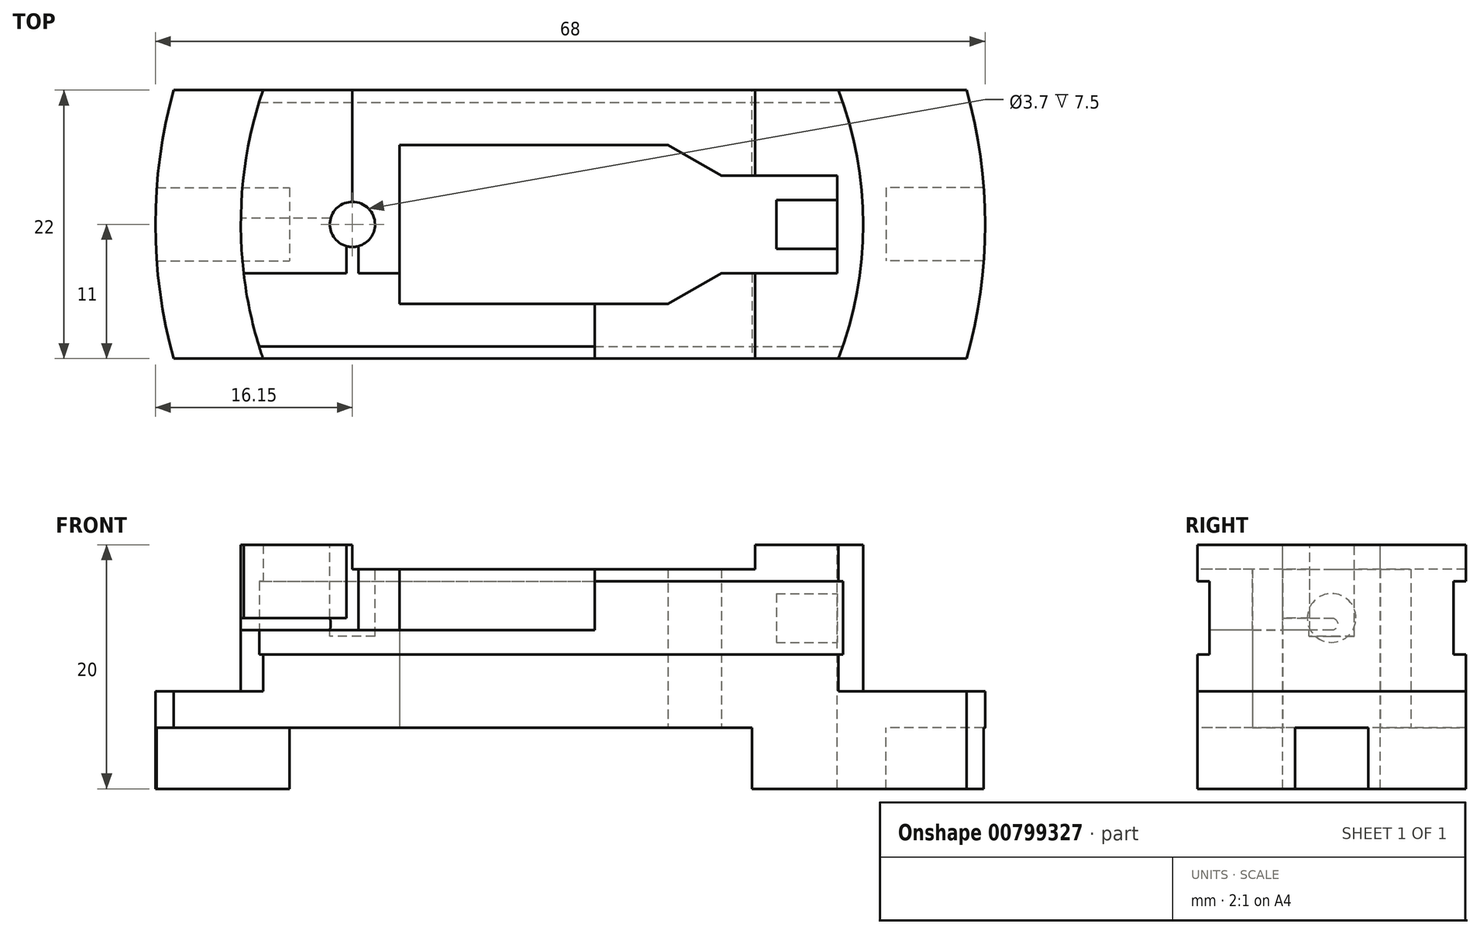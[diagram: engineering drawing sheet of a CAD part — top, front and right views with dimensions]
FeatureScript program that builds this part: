
annotation { "Feature Type Name" : "Feature", "Feature Type Description" : "" }
export const myFeature = defineFeature(function(context is Context, id is Id, definition is map)
    precondition{}
    {
        {
            var Q0;
            Q0=qCreatedBy(makeId("Top.planeOp"),FACE);
            var sketch = newSketch(context, id + "F0", { "sketchPlane" : qUnion([Q0])});
            skLineSegment(sketch, "E0.bottom", {"start": v(32.5, 11) * mm, "end": v(-32.5, 11) * mm});
            skLineSegment(sketch, "E0.top", {"start": v(32.5, -11) * mm, "end": v(-32.5, -11) * mm});
            skLineSegment(sketch, "E0.left", {"start": v(32.5, 11) * mm, "end": v(32.5, -11) * mm, "construction": true});
            skLineSegment(sketch, "E0.right", {"start": v(-32.5, 11) * mm, "end": v(-32.5, -11) * mm, "construction": true});
            skPoint(sketch, "E0.middle", {"position": v(0, 0) * mm});
            skArc(sketch, "E1", {"start": v(-32.5, 11) * mm, "mid": v(-34, 0) * mm, "end": v(-32.5, -11) * mm});
            skArc(sketch, "E2", {"start": v(32.5, -11) * mm, "mid": v(34, 0) * mm, "end": v(32.5, 11) * mm});
            skSolve(sketch);
        }
        {
            var Q0;
            Q0 = qSketchRegion(id + "F0", true);
            var Q1;
            Q1 = qConstructionFilter(qBodyType(qCreatedBy(id + "F0" ,EDGE), BodyType.WIRE), ConstructionObject.NO);
            extrude(context, id + "F1", {"entities" : qUnion([Q0]), "surfaceEntities" : qUnion([Q1]), "oppositeDirection" : true, "depth" : 3 * mm, "offsetDistance" : 25 * mm});
        }
        {
            var Q0;
            Q0=makeQuery(id+"F1.opExtrude","CAP_FACE",FACE,{"disambiguationData":[OSD([sQuery(id+"F0.wireOp",EDGE,"E0.bottom"),sQuery(id+"F0.wireOp",EDGE,"E0.top"),sQuery(id+"F0.wireOp",EDGE,"E1"),sQuery(id+"F0.wireOp",EDGE,"E2")])],"isStart":false});
            var sketch = newSketch(context, id + "F2", { "sketchPlane" : qUnion([Q0])});
            skLineSegment(sketch, "E3", {"start": v(33.9, 3) * mm, "end": v(25.9, 3) * mm});
            skLineSegment(sketch, "E4", {"start": v(25.9, 3) * mm, "end": v(25.9, 0) * mm});
            skLineSegment(sketch, "E5", {"start": v(21.9, 0) * mm, "end": v(21.9, 4) * mm});
            skLineSegment(sketch, "E6", {"start": v(21.9, 4) * mm, "end": v(14.9, 4) * mm});
            skLineSegment(sketch, "E7", {"start": v(14.9, 4) * mm, "end": v(14.9, 11) * mm});
            skLineSegment(sketch, "E8", {"start": v(-33.9, 3) * mm, "end": v(-23, 3) * mm});
            skLineSegment(sketch, "E9", {"start": v(-23, 3) * mm, "end": v(-23, 0) * mm});
            skLineSegment(sketch, "E10.0", {"start": v(32.5, 11) * mm, "end": v(14.9, 11) * mm});
            skArc(sketch, "E11.0", {"start": v(32.5, 11) * mm, "mid": v(33.4, 7.03) * mm, "end": v(33.9, 3) * mm});
            skArc(sketch, "E12.0", {"start": v(-32.5, -11) * mm, "mid": v(-34, 0) * mm, "end": v(-32.5, 11) * mm});
            skLineSegment(sketch, "E13.0", {"start": v(32.5, -11) * mm, "end": v(14.9, -11) * mm});
            skLineSegment(sketch, "E14.MirrorCS", {"start": v(-33.9, -3) * mm, "end": v(-23, -3) * mm});
            skLineSegment(sketch, "E15.MirrorCS", {"start": v(-23, -3) * mm, "end": v(-23, 0) * mm});
            skLineSegment(sketch, "E16.MirrorCS", {"start": v(14.9, -4) * mm, "end": v(14.9, -11) * mm});
            skLineSegment(sketch, "E17.MirrorCS", {"start": v(21.9, -4) * mm, "end": v(14.9, -4) * mm});
            skLineSegment(sketch, "E18.MirrorCS", {"start": v(21.9, 0) * mm, "end": v(21.9, -4) * mm});
            skLineSegment(sketch, "E19.MirrorCS", {"start": v(25.9, -3) * mm, "end": v(25.9, 0) * mm});
            skLineSegment(sketch, "E20.MirrorCS", {"start": v(33.9, -3) * mm, "end": v(25.9, -3) * mm});
            skArc(sketch, "E21.trimOffspring", {"start": v(33.9, -3) * mm, "mid": v(33.4, -7.03) * mm, "end": v(32.5, -11) * mm});
            skSolve(sketch);
        }
        {
            var Q0;
            {var subQ2=sQuery(id+"F2.wireOp",EDGE,"E8");Q0=makeQuery(id+"F2.imprint","IMPRINT",FACE,{"disambiguationData":[TD([[makeQuery(id+"F2.imprint","IMPRINT",EDGE,{"derivedFrom":subQ2}),-1.0]])]});}
            var Q1;
            Q1=makeQuery(id+"F2.imprint","IMPRINT",FACE,{"disambiguationData":[TD([[makeQuery(id+"F2.imprint","IMPRINT",EDGE,{"derivedFrom":sQuery(id+"F2.wireOp",EDGE,"E3")}),-1.0]])]});
            extrude(context, id + "F3", {"entities" : qUnion([Q0, Q1]), "operationType" : NewBodyOperationType.ADD, "depth" : 5 * mm, "offsetDistance" : 25 * mm});
        }
        {
            var Q0;
            {var subQ0=sQuery(id+"F0.wireOp",EDGE,"E0.bottom");var subQ1=sQuery(id+"F0.wireOp",EDGE,"E0.top");var subQ2=sQuery(id+"F0.wireOp",EDGE,"E1");Q0=makeQuery(id+"F3.boolean.opBoolean","SPLIT",FACE,{"disambiguationData":[TD([makeQuery(id+"F1.opExtrude","SWEPT_FACE",FACE,{"disambiguationData":[OSD([subQ0])]})])],"derivedFrom":makeQuery(id+"F1.opExtrude","CAP_FACE",FACE,{"disambiguationData":[OSD([subQ0,subQ1,subQ2,sQuery(id+"F0.wireOp",EDGE,"E2")])],"isStart":false})});}
            var sketch = newSketch(context, id + "F4", { "sketchPlane" : qUnion([Q0])});
            skLineSegment(sketch, "E22.0", {"start": v(21.9, 4) * mm, "end": v(14.9, 4) * mm});
            skLineSegment(sketch, "E23.0", {"start": v(21.9, -4) * mm, "end": v(21.9, 4) * mm});
            skLineSegment(sketch, "E24.0", {"start": v(21.9, -4) * mm, "end": v(14.9, -4) * mm});
            skLineSegment(sketch, "E25", {"start": v(-14, 0) * mm, "end": v(-14, 6.5) * mm});
            skLineSegment(sketch, "E26", {"start": v(-14, 6.5) * mm, "end": v(8, 6.5) * mm});
            skLineSegment(sketch, "E27", {"start": v(8, 6.5) * mm, "end": v(12.4, 4) * mm});
            skLineSegment(sketch, "E28", {"start": v(12.4, 4) * mm, "end": v(14.9, 4) * mm});
            skLineSegment(sketch, "E29.MirrorCS", {"start": v(-14, 0) * mm, "end": v(-14, -6.5) * mm});
            skLineSegment(sketch, "E30.MirrorCS", {"start": v(-14, -6.5) * mm, "end": v(8, -6.5) * mm});
            skLineSegment(sketch, "E31.MirrorCS", {"start": v(8, -6.5) * mm, "end": v(12.4, -4) * mm});
            skLineSegment(sketch, "E32.MirrorCS", {"start": v(12.4, -4) * mm, "end": v(14.9, -4) * mm});
            skSolve(sketch);
        }
        {
            var Q0;
            Q0=makeQuery(id+"F4.imprint","IMPRINT",FACE,{"disambiguationData":[TD([[makeQuery(id+"F4.imprint","IMPRINT",EDGE,{"derivedFrom":sQuery(id+"F4.wireOp",EDGE,"E22.0")}),1.0]])]});
            extrude(context, id + "F5", {"entities" : qUnion([Q0]), "operationType" : NewBodyOperationType.REMOVE, "endBound" : BoundingType.THROUGH_ALL, "oppositeDirection" : true, "depth" : 25 * mm, "offsetDistance" : 25 * mm});
        }
        {
            var Q0;
            Q0=makeQuery(id+"F1.opExtrude","CAP_FACE",FACE,{"disambiguationData":[OSD([sQuery(id+"F0.wireOp",EDGE,"E0.bottom"),sQuery(id+"F0.wireOp",EDGE,"E0.top"),sQuery(id+"F0.wireOp",EDGE,"E1"),sQuery(id+"F0.wireOp",EDGE,"E2")])],"isStart":true});
            var sketch = newSketch(context, id + "F6", { "sketchPlane" : qUnion([Q0])});
            skArc(sketch, "E33", {"start": v(-25.18, 11) * mm, "mid": v(-27, 0) * mm, "end": v(-25.18, -11) * mm});
            skArc(sketch, "E34", {"start": v(21.99, -11) * mm, "mid": v(24, 0) * mm, "end": v(21.99, 11) * mm});
            skLineSegment(sketch, "E35.0", {"start": v(21.99, 11) * mm, "end": v(-25.18, 11) * mm});
            skLineSegment(sketch, "E36.0", {"start": v(21.99, -11) * mm, "end": v(-25.18, -11) * mm});
            skPoint(sketch, "E37.orphan", {"position": v(-32.5, 11) * mm});
            skPoint(sketch, "E38.orphan", {"position": v(32.5, 11) * mm});
            skPoint(sketch, "E39.orphan", {"position": v(32.5, -11) * mm});
            skPoint(sketch, "E40.orphan", {"position": v(-32.5, -11) * mm});
            skSolve(sketch);
        }
        {
            var Q0;
            Q0=makeQuery(id+"F6.imprint","IMPRINT",FACE,{"disambiguationData":[TD([[makeQuery(id+"F6.imprint","IMPRINT",EDGE,{"derivedFrom":sQuery(id+"F6.wireOp",EDGE,"E33")}),1.0]])]});
            extrude(context, id + "F7", {"entities" : qUnion([Q0]), "operationType" : NewBodyOperationType.ADD, "depth" : 12 * mm, "offsetDistance" : 25 * mm});
        }
        {
            var Q0;
            Q0=qCreatedBy(makeId("Right.planeOp"),FACE);
            var sketch = newSketch(context, id + "F8", { "sketchPlane" : qUnion([Q0])});
            skLineSegment(sketch, "E41.0", {"start": v(-11, 9) * mm, "end": v(-11, 3) * mm});
            skLineSegment(sketch, "E42.0", {"start": v(11, 9) * mm, "end": v(11, 3) * mm});
            skLineSegment(sketch, "E43", {"start": v(-11, 9) * mm, "end": v(-10, 9) * mm});
            skLineSegment(sketch, "E44", {"start": v(-10, 9) * mm, "end": v(-10, 3) * mm});
            skLineSegment(sketch, "E45", {"start": v(-10, 3) * mm, "end": v(-11, 3) * mm});
            skPoint(sketch, "E46.orphan", {"position": v(-11, 12) * mm});
            skPoint(sketch, "E47.orphan", {"position": v(-11, 0) * mm});
            skLineSegment(sketch, "E48.MirrorCS", {"start": v(11, 9) * mm, "end": v(10, 9) * mm});
            skLineSegment(sketch, "E49.MirrorCS", {"start": v(10, 9) * mm, "end": v(10, 3) * mm});
            skLineSegment(sketch, "E50.MirrorCS", {"start": v(10, 3) * mm, "end": v(11, 3) * mm});
            skPoint(sketch, "E51.orphan", {"position": v(11, 12) * mm});
            skPoint(sketch, "E52.orphan", {"position": v(11, 0) * mm});
            skSolve(sketch);
        }
        {
            var Q0;
            Q0 = qSketchRegion(id + "F8", true);
            extrude(context, id + "F9", {"entities" : qUnion([Q0]), "operationType" : NewBodyOperationType.REMOVE, "endBound" : BoundingType.THROUGH_ALL, "oppositeDirection" : true, "depth" : 25 * mm, "offsetDistance" : 25 * mm, "hasSecondDirection" : true, "secondDirectionBound" : SecondDirectionBoundingType.THROUGH_ALL, "secondDirectionOppositeDirection" : false, "secondDirectionDepth" : 25 * mm});
        }
        {
            var Q0;
            Q0=makeQuery(id+"F7.opExtrude","CAP_FACE",FACE,{"disambiguationData":[OSD([sQuery(id+"F0.wireOp",EDGE,"E0.bottom"),sQuery(id+"F0.wireOp",EDGE,"E0.top"),sQuery(id+"F0.wireOp",EDGE,"E1"),sQuery(id+"F0.wireOp",EDGE,"E2"),sQuery(id+"F4.wireOp",EDGE,"E22.0"),sQuery(id+"F4.wireOp",EDGE,"E23.0"),sQuery(id+"F4.wireOp",EDGE,"E24.0"),sQuery(id+"F4.wireOp",EDGE,"E25"),sQuery(id+"F4.wireOp",EDGE,"E26"),sQuery(id+"F4.wireOp",EDGE,"E27"),sQuery(id+"F4.wireOp",EDGE,"E28"),sQuery(id+"F4.wireOp",EDGE,"E29.MirrorCS"),sQuery(id+"F4.wireOp",EDGE,"E30.MirrorCS"),sQuery(id+"F4.wireOp",EDGE,"E31.MirrorCS"),sQuery(id+"F4.wireOp",EDGE,"E32.MirrorCS"),sQuery(id+"F6.wireOp",EDGE,"E33"),sQuery(id+"F6.wireOp",EDGE,"E34"),sQuery(id+"F6.wireOp",EDGE,"E35.0"),sQuery(id+"F6.wireOp",EDGE,"E36.0")])],"isStart":false});
            var sketch = newSketch(context, id + "F10", { "sketchPlane" : qUnion([Q0])});
            skCircle(sketch, "E53", {"center": v(-17.85, 0) * mm, "radius": 1.85 * mm});
            skSolve(sketch);
        }
        {
            var Q0;
            Q0=makeQuery(id+"F10.imprint","IMPRINT",FACE,{"disambiguationData":[TD([[makeQuery(id+"F10.imprint","IMPRINT",EDGE,{"derivedFrom":sQuery(id+"F10.wireOp",EDGE,"E53")}),1.0]])]});
            extrude(context, id + "F11", {"entities" : qUnion([Q0]), "operationType" : NewBodyOperationType.REMOVE, "oppositeDirection" : true, "depth" : 7.5 * mm, "offsetDistance" : 25 * mm});
        }
        {
            var Q0;
            Q0=makeQuery(id+"F7.opExtrude","CAP_FACE",FACE,{"disambiguationData":[OSD([sQuery(id+"F0.wireOp",EDGE,"E0.bottom"),sQuery(id+"F0.wireOp",EDGE,"E0.top"),sQuery(id+"F0.wireOp",EDGE,"E1"),sQuery(id+"F0.wireOp",EDGE,"E2"),sQuery(id+"F4.wireOp",EDGE,"E22.0"),sQuery(id+"F4.wireOp",EDGE,"E23.0"),sQuery(id+"F4.wireOp",EDGE,"E24.0"),sQuery(id+"F4.wireOp",EDGE,"E25"),sQuery(id+"F4.wireOp",EDGE,"E26"),sQuery(id+"F4.wireOp",EDGE,"E27"),sQuery(id+"F4.wireOp",EDGE,"E28"),sQuery(id+"F4.wireOp",EDGE,"E29.MirrorCS"),sQuery(id+"F4.wireOp",EDGE,"E30.MirrorCS"),sQuery(id+"F4.wireOp",EDGE,"E31.MirrorCS"),sQuery(id+"F4.wireOp",EDGE,"E32.MirrorCS"),sQuery(id+"F6.wireOp",EDGE,"E33"),sQuery(id+"F6.wireOp",EDGE,"E34"),sQuery(id+"F6.wireOp",EDGE,"E35.0"),sQuery(id+"F6.wireOp",EDGE,"E36.0")])],"isStart":false});
            var sketch = newSketch(context, id + "F12", { "sketchPlane" : qUnion([Q0])});
            skLineSegment(sketch, "E54.bottom", {"start": v(-17.85, 11) * mm, "end": v(15.15, 11) * mm});
            skLineSegment(sketch, "E54.top", {"start": v(-17.85, -11) * mm, "end": v(15.15, -11) * mm});
            skLineSegment(sketch, "E54.left", {"start": v(-17.85, 11) * mm, "end": v(-17.85, -11) * mm});
            skLineSegment(sketch, "E54.right", {"start": v(15.15, 11) * mm, "end": v(15.15, -11) * mm});
            skPoint(sketch, "E55", {"position": v(-17.85, 0) * mm});
            skLineSegment(sketch, "E56.bottom", {"start": v(-27, -4) * mm, "end": v(2, -4) * mm});
            skLineSegment(sketch, "E56.top", {"start": v(-27, -11) * mm, "end": v(2, -11) * mm});
            skLineSegment(sketch, "E56.left", {"start": v(-27, -4) * mm, "end": v(-27, -11) * mm});
            skLineSegment(sketch, "E56.right", {"start": v(2, -4) * mm, "end": v(2, -11) * mm});
            skLineSegment(sketch, "E57", {"start": v(-17.85, 0) * mm, "end": v(-18.35, 0) * mm});
            skLineSegment(sketch, "E58", {"start": v(-18.35, 0) * mm, "end": v(-18.35, -4) * mm});
            skLineSegment(sketch, "E59.MirrorCS", {"start": v(-17.35, 0) * mm, "end": v(-17.35, -4) * mm});
            skLineSegment(sketch, "E60.MirrorCS", {"start": v(-17.85, 0) * mm, "end": v(-17.35, 0) * mm});
            skSolve(sketch);
        }
        {
            var Q0;
            {var subQ1=sQuery(id+"F12.wireOp",EDGE,"E54.bottom");Q0=makeQuery(id+"F12.imprint","IMPRINT",FACE,{"disambiguationData":[TD([[makeQuery(id+"F12.imprint","IMPRINT",EDGE,{"derivedFrom":subQ1}),1.0]])]});}
            var Q1;
            {var subQ1=sQuery(id+"F12.wireOp",EDGE,"E56.top");var subQ9=sQuery(id+"F12.wireOp",EDGE,"E54.left");var subQ10=makeQuery(id+"F12.imprint","INTERSECT",VERTEX,{"derivedFrom":[subQ9,subQ1]});Q1=makeQuery(id+"F12.imprint","IMPRINT",FACE,{"disambiguationData":[TD([[makeQuery(id+"F12.imprint","IMPRINT",EDGE,{"disambiguationData":[TD([[subQ10,1.0]])],"derivedFrom":subQ9}),1.0]])]});}
            var Q2;
            {var subQ6=sQuery(id+"F12.wireOp",EDGE,"E54.top");Q2=makeQuery(id+"F12.imprint","IMPRINT",FACE,{"disambiguationData":[TD([[makeQuery(id+"F12.imprint","IMPRINT",EDGE,{"derivedFrom":subQ6}),-1.0]])]});}
            extrude(context, id + "F13", {"entities" : qUnion([Q0, Q1, Q2]), "operationType" : NewBodyOperationType.REMOVE, "oppositeDirection" : true, "depth" : 2 * mm, "offsetDistance" : 25 * mm});
        }
        {
            var Q0;
            {var subQ1=sQuery(id+"F12.wireOp",EDGE,"E56.top");var subQ9=sQuery(id+"F12.wireOp",EDGE,"E54.left");var subQ10=makeQuery(id+"F12.imprint","INTERSECT",VERTEX,{"derivedFrom":[subQ9,subQ1]});Q0=makeQuery(id+"F12.imprint","IMPRINT",FACE,{"disambiguationData":[TD([[makeQuery(id+"F12.imprint","IMPRINT",EDGE,{"disambiguationData":[TD([[subQ10,1.0]])],"derivedFrom":subQ9}),1.0]])]});}
            var Q1;
            {var subQ0=sQuery(id+"F12.wireOp",EDGE,"E56.top");var subQ1=sQuery(id+"F12.wireOp",EDGE,"E54.left");var subQ2=makeQuery(id+"F12.imprint","INTERSECT",VERTEX,{"derivedFrom":[subQ1,subQ0]});Q1=makeQuery(id+"F12.imprint","IMPRINT",FACE,{"disambiguationData":[TD([[makeQuery(id+"F12.imprint","IMPRINT",EDGE,{"disambiguationData":[TD([[subQ2,1.0]])],"derivedFrom":subQ1}),-1.0]])]});}
            var Q2;
            {var subQ0=sQuery(id+"F12.wireOp",EDGE,"E56.bottom");var subQ1=sQuery(id+"F12.wireOp",EDGE,"E54.left");var subQ2=makeQuery(id+"F12.imprint","INTERSECT",VERTEX,{"derivedFrom":[subQ1,subQ0]});Q2=makeQuery(id+"F12.imprint","IMPRINT",FACE,{"disambiguationData":[TD([[makeQuery(id+"F12.imprint","IMPRINT",EDGE,{"disambiguationData":[TD([[subQ2,1.0]])],"derivedFrom":subQ1}),1.0]])]});}
            var Q3;
            {var subQ0=sQuery(id+"F12.wireOp",EDGE,"E56.bottom");var subQ1=sQuery(id+"F12.wireOp",EDGE,"E54.left");var subQ2=makeQuery(id+"F12.imprint","INTERSECT",VERTEX,{"derivedFrom":[subQ1,subQ0]});Q3=makeQuery(id+"F12.imprint","IMPRINT",FACE,{"disambiguationData":[TD([[makeQuery(id+"F12.imprint","IMPRINT",EDGE,{"disambiguationData":[TD([[subQ2,1.0]])],"derivedFrom":subQ1}),-1.0]])]});}
            extrude(context, id + "F14", {"entities" : qUnion([Q0, Q1, Q2, Q3]), "operationType" : NewBodyOperationType.REMOVE, "oppositeDirection" : true, "depth" : 7 * mm, "offsetDistance" : 25 * mm});
        }
        {
            var Q0;
            Q0=makeQuery(id+"F1.opExtrude","CAP_EDGE",EDGE,{"disambiguationData":[OSD([sQuery(id+"F0.wireOp",EDGE,"E1")])],"isStart":true});
            cPoint(context, id + "F15", {"entities" : qUnion([Q0]), "parameter" : 0.5});
        }
        {
            var Q0;
            Q0=qCreatedBy(makeId("Right.planeOp"),FACE);
            var Q1;
            Q1 = qCreatedBy(id + "F15" ,VERTEX);
            cPlane(context, id + "F16", {"entities" : qUnion([Q0, Q1]), "cplaneType" : CPlaneType.PLANE_POINT, "offset" : 25 * mm, "width" : 150 * mm, "height" : 150 * mm});
        }
        {
            var Q0;
            Q0=qCreatedBy(id+"F16.planeOp",FACE);
            var sketch = newSketch(context, id + "F17", { "sketchPlane" : qUnion([Q0])});
            skLineSegment(sketch, "E61.0", {"start": v(-4, 5) * mm, "end": v(-10, 5) * mm});
            skLineSegment(sketch, "E62", {"start": v(-4, 5) * mm, "end": v(0, 5) * mm});
            skArc(sketch, "E63", {"start": v(0, 5) * mm, "mid": v(0.5, 5.5) * mm, "end": v(0, 6) * mm});
            skLineSegment(sketch, "E64", {"start": v(0, 6) * mm, "end": v(-4, 6) * mm});
            skLineSegment(sketch, "E65", {"start": v(-4, 6) * mm, "end": v(-4, 5) * mm});
            skSolve(sketch);
        }
        {
            var Q0;
            Q0 = qSketchRegion(id + "F17", true);
            var Q1;
            Q1=makeQuery(id+"F14.boolean.opBoolean","COPY",FACE,{"derivedFrom":makeQuery(id+"F14.opExtrude","SWEPT_FACE",FACE,{"disambiguationData":[OSD([sQuery(id+"F12.wireOp",EDGE,"E59.MirrorCS")])]})});
            extrude(context, id + "F18", {"entities" : qUnion([Q0]), "operationType" : NewBodyOperationType.REMOVE, "endBound" : BoundingType.UP_TO_SURFACE, "depth" : 25 * mm, "endBoundEntityFace" : qUnion([Q1]), "offsetDistance" : 25 * mm});
        }
        {
            var Q0;
            {var subQ0=sQuery(id+"F4.wireOp",EDGE,"E23.0");Q0=makeQuery(id+"F7.boolean.opBoolean","MERGE",FACE,{"derivedFrom":[makeQuery(id+"F5.boolean.opBoolean","MERGE",FACE,{"derivedFrom":[makeQuery(id+"F3.opExtrude","SWEPT_FACE",FACE,{"disambiguationData":[OSD([sQuery(id+"F2.wireOp",EDGE,"E5"),sQuery(id+"F2.wireOp",EDGE,"E18.MirrorCS")])]}),makeQuery(id+"F5.opExtrude","SWEPT_FACE",FACE,{"disambiguationData":[OSD([subQ0])]})]}),makeQuery(id+"F7.opExtrude","SWEPT_FACE",FACE,{"disambiguationData":[OSD([sQuery(id+"F0.wireOp",EDGE,"E0.bottom"),sQuery(id+"F0.wireOp",EDGE,"E0.top"),sQuery(id+"F0.wireOp",EDGE,"E1"),sQuery(id+"F0.wireOp",EDGE,"E2"),subQ0])]})]});}
            var sketch = newSketch(context, id + "F19", { "sketchPlane" : qUnion([Q0])});
            skCircle(sketch, "E66", {"center": v(0, 6) * mm, "radius": 2 * mm});
            skSolve(sketch);
        }
        {
            var Q0;
            Q0 = qSketchRegion(id + "F19", true);
            extrude(context, id + "F20", {"entities" : qUnion([Q0]), "operationType" : NewBodyOperationType.ADD, "depth" : 5 * mm, "offsetDistance" : 25 * mm});
        }
    });
